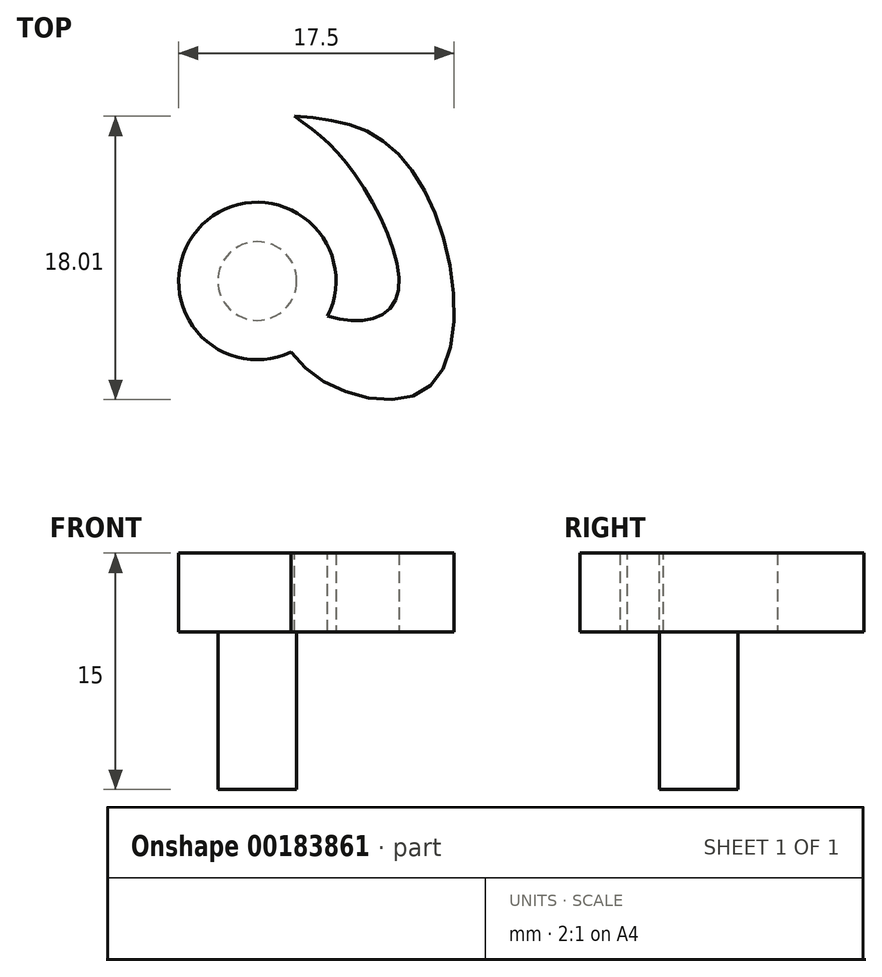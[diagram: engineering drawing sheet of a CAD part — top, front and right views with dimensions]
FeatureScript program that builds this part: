
annotation { "Feature Type Name" : "Feature", "Feature Type Description" : "" }
export const myFeature = defineFeature(function(context is Context, id is Id, definition is map)
    precondition{}
    {
        {
            var Q0;
            Q0=qCreatedBy(makeId("Top.planeOp"),FACE);
            var sketch = newSketch(context, id + "F0", { "sketchPlane" : qUnion([Q0])});
            skCircle(sketch, "E0", {"center": v(0, 0) * mm, "radius": 2.5 * mm});
            skSolve(sketch);
        }
        {
            var Q0;
            Q0 = qSketchRegion(id + "F0", true);
            extrude(context, id + "F1", {"entities" : qUnion([Q0]), "depth" : 10 * mm});
        }
        {
            var Q0;
            Q0=makeQuery(id+"F1.opExtrude","CAP_FACE",FACE,{"disambiguationData":[OSD([sQuery(id+"F0.wireOp",EDGE,"E0")])],"isStart":false});
            var sketch = newSketch(context, id + "F2", { "sketchPlane" : qUnion([Q0])});
            skCircle(sketch, "E1", {"center": v(0, 0) * mm, "radius": 5 * mm});
            skSolve(sketch);
        }
        {
            var Q0;
            Q0 = qSketchRegion(id + "F2", true);
            extrude(context, id + "F3", {"entities" : qUnion([Q0]), "operationType" : NewBodyOperationType.ADD, "depth" : 5 * mm});
        }
        {
            var Q0;
            Q0=makeQuery(id+"F3.opExtrude","CAP_FACE",FACE,{"disambiguationData":[OSD([sQuery(id+"F2.wireOp",EDGE,"E1")])],"isStart":false});
            var sketch = newSketch(context, id + "F4", { "sketchPlane" : qUnion([Q0])});
            skFitSpline(sketch, "E2", {"points": [v(0, 0) * mm, v(3.64, -6) * mm, v(10.85, -6.77) * mm, v(11.89, 2.53) * mm, v(7.53, 9.21) * mm, v(2.37, 10.47) * mm], "startDerivative": vector(12.24, -34.7) * mm, "endDerivative": vector(-31.6, 2.71) * mm});
            skFitSpline(sketch, "E3", {"points": [v(2.37, 10.47) * mm, v(6.15, 6.87) * mm, v(8.9, -0.91) * mm, v(5.99, -2.52) * mm, v(0, 0) * mm], "startDerivative": vector(15.6, -11.36) * mm, "endDerivative": vector(-23.12, 13.56) * mm});
            skSolve(sketch);
        }
        {
            var Q0;
            Q0 = qSketchRegion(id + "F4", true);
            extrude(context, id + "F5", {"entities" : qUnion([Q0]), "operationType" : NewBodyOperationType.ADD, "oppositeDirection" : true, "depth" : 5 * mm});
        }
    });
